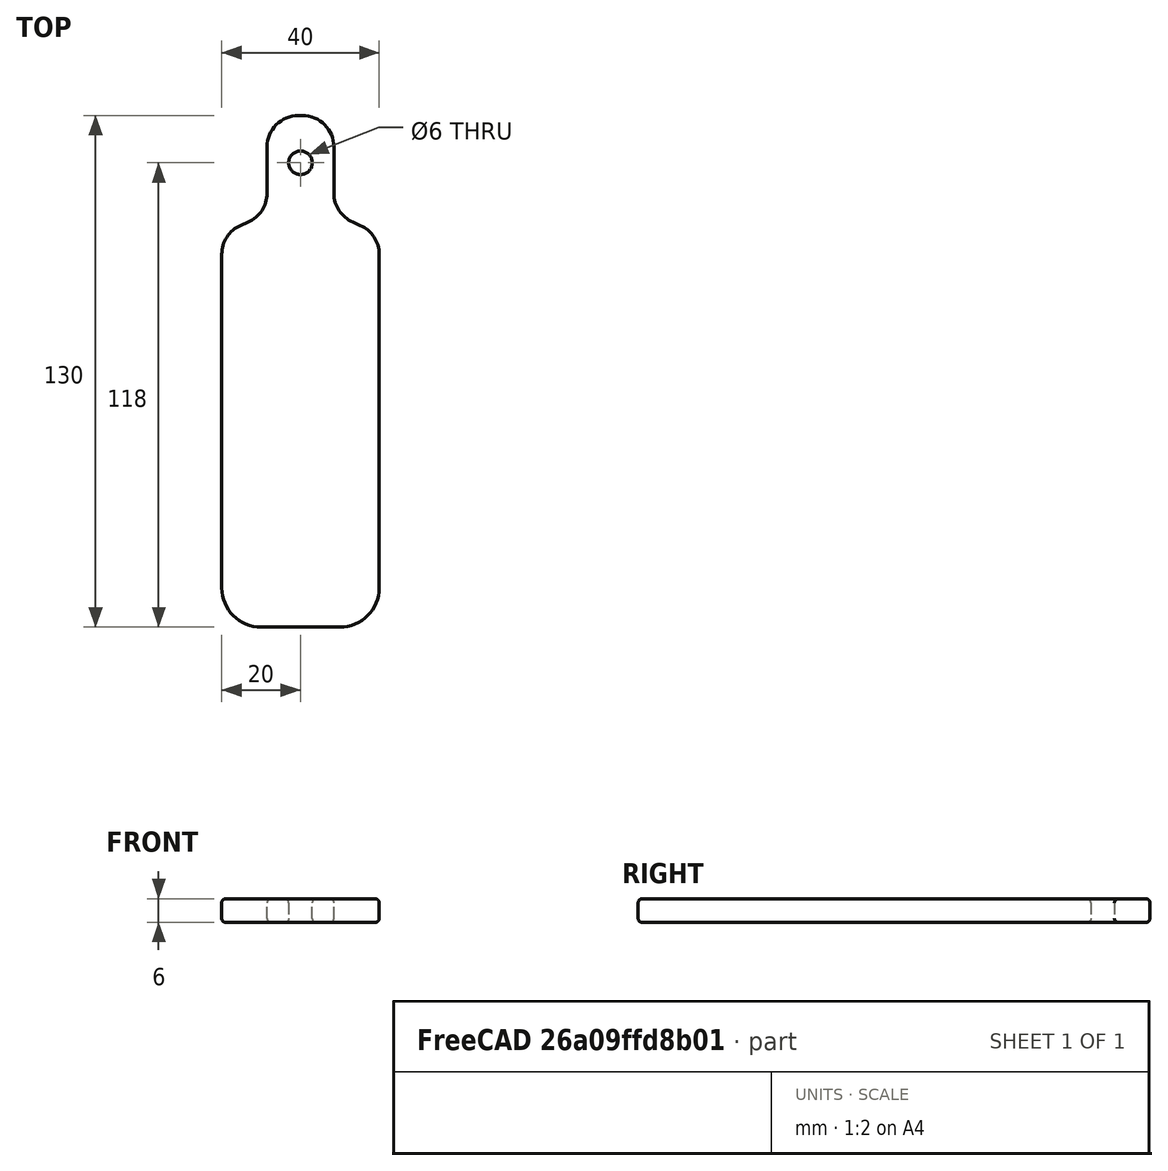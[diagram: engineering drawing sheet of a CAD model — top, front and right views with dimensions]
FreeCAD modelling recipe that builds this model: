
FCSTD DOCUMENT  (FreeCAD 1.1R20260325 (Git shallow))
Label: edfger
License: All rights reserved
LicenseURL: http://en.wikipedia.org/wiki/All_rights_reserved
objects: PartDesign::Fillet×3, App::Point×2, Sketcher::SketchObject×1, PartDesign::Pad×1, PartDesign::Body×1, App::Part×1, Mesh::Feature×1
note: 15 computed .brp shape members not serialized (recipe doc carries the construction recipe); baked Part::Feature solids carry a one-line shape summary decoded from their .brp

FEATURE [App::Point] Origin001
  Role = Origin
FEATURE [App::Point] Origin003
  Role = Origin
FEATURE [Sketcher::SketchObject] Sketch
  ArcFitTolerance = 1e-06
  AttachmentSupport = -> [Origin002]
  ExternalTypes = [0]
  FullyConstrained = true
  MakeInternals = false
  MapMode = 5
  _ExternalGeoVersion = 1
  sketch-geometry (9):
    g0: LineSegment StartX=-20 StartY=50 StartZ=0 EndX=-20 EndY=-50 EndZ=0
    g1: LineSegment StartX=-20 StartY=-50 StartZ=0 EndX=20 EndY=-50 EndZ=0
    g2: LineSegment StartX=20 StartY=-50 StartZ=0 EndX=20 EndY=50 EndZ=0
    g3: LineSegment StartX=20 StartY=50 StartZ=0 EndX=8.5 EndY=55 EndZ=0
    g4: LineSegment StartX=8.5 StartY=55 StartZ=0 EndX=8.5 EndY=80 EndZ=0
    g5: LineSegment StartX=8.5 StartY=80 StartZ=0 EndX=-8.5 EndY=80 EndZ=0
    g6: LineSegment StartX=-8.5 StartY=80 StartZ=0 EndX=-8.5 EndY=55 EndZ=0
    g7: LineSegment StartX=-8.5 StartY=55 StartZ=0 EndX=-20 EndY=50 EndZ=0
    g8: Circle CenterX=0 CenterY=68 CenterZ=0 NormalX=0 NormalY=0 NormalZ=1 AngleXU=0 Radius=3
  constraints (24):
    c: Vertical(g0)
    c: Coincident(g1,g0)
    c: Coincident(g2,g1)
    c: Coincident(g4,g3)
    c: Vertical(g4)
    c: Coincident(g5,g4)
    c: Horizontal(g5)
    c: Coincident(g6,g5)
    c: Vertical(g6)
    c: Coincident(g7,g6)
    c: Equal(g7,g3)
    c: Symmetric(g0,g1,g-2)
    c: Symmetric(g6,g3,g-2)
    c: Coincident(g7,g0)
    c: Coincident(g3,g2)
    c: DistanceY(g0,g0) = 100
    c: DistanceY(g6,g6) = 25
    c: DistanceX(g1,g1) = 40
    c: DistanceX(g5,g5) = 17
    c: Symmetric(g2,g1,g-1)
    c: DistanceY(g0,g6) = 5
    c: PointOnObject(g8,g-2)
    c: Diameter(g8) = 6
    c: DistanceY(g8,g5) = 12
FEATURE [PartDesign::Pad] Pad
  Direction = (0,0,1)
  Length = 6
  Length2 = 10
  Profile = -> Sketch
  ReferenceAxis = -> Sketch [N_Axis]
  SideType = 0
  Suppressed = false
  Type = 0
  Type2 = 0
FEATURE [PartDesign::Fillet] Fillet
  Base = -> Pad [Edge8,Edge11,Edge1,Edge17,Edge14,Edge20]
  BaseFeature = -> Pad
  Radius = 8
  SupportTransform = false
  Suppressed = false
  UseAllEdges = false
FEATURE [PartDesign::Fillet] Fillet001
  Base = -> Fillet [Edge21,Edge3]
  BaseFeature = -> Fillet
  Radius = 10
  SupportTransform = false
  Suppressed = false
  UseAllEdges = false
FEATURE [PartDesign::Fillet] Fillet002
  Base = -> Fillet001 [Edge38,Edge20,Edge4,Edge11]
  BaseFeature = -> Fillet001
  Radius = 1
  SupportTransform = false
  Suppressed = false
  UseAllEdges = false
FEATURE [PartDesign::Body] Body
  AllowCompound = true
  Group = -> [Sketch,Pad,Fillet,Fillet001,Fillet002]
  Origin = -> Origin002
  Tip = -> Fillet002
FEATURE [App::Part] Part
  Group = -> [Body]
  Origin = -> Origin
FEATURE [Mesh::Feature] Mesh  label="Fillet002 (Meshed)"
